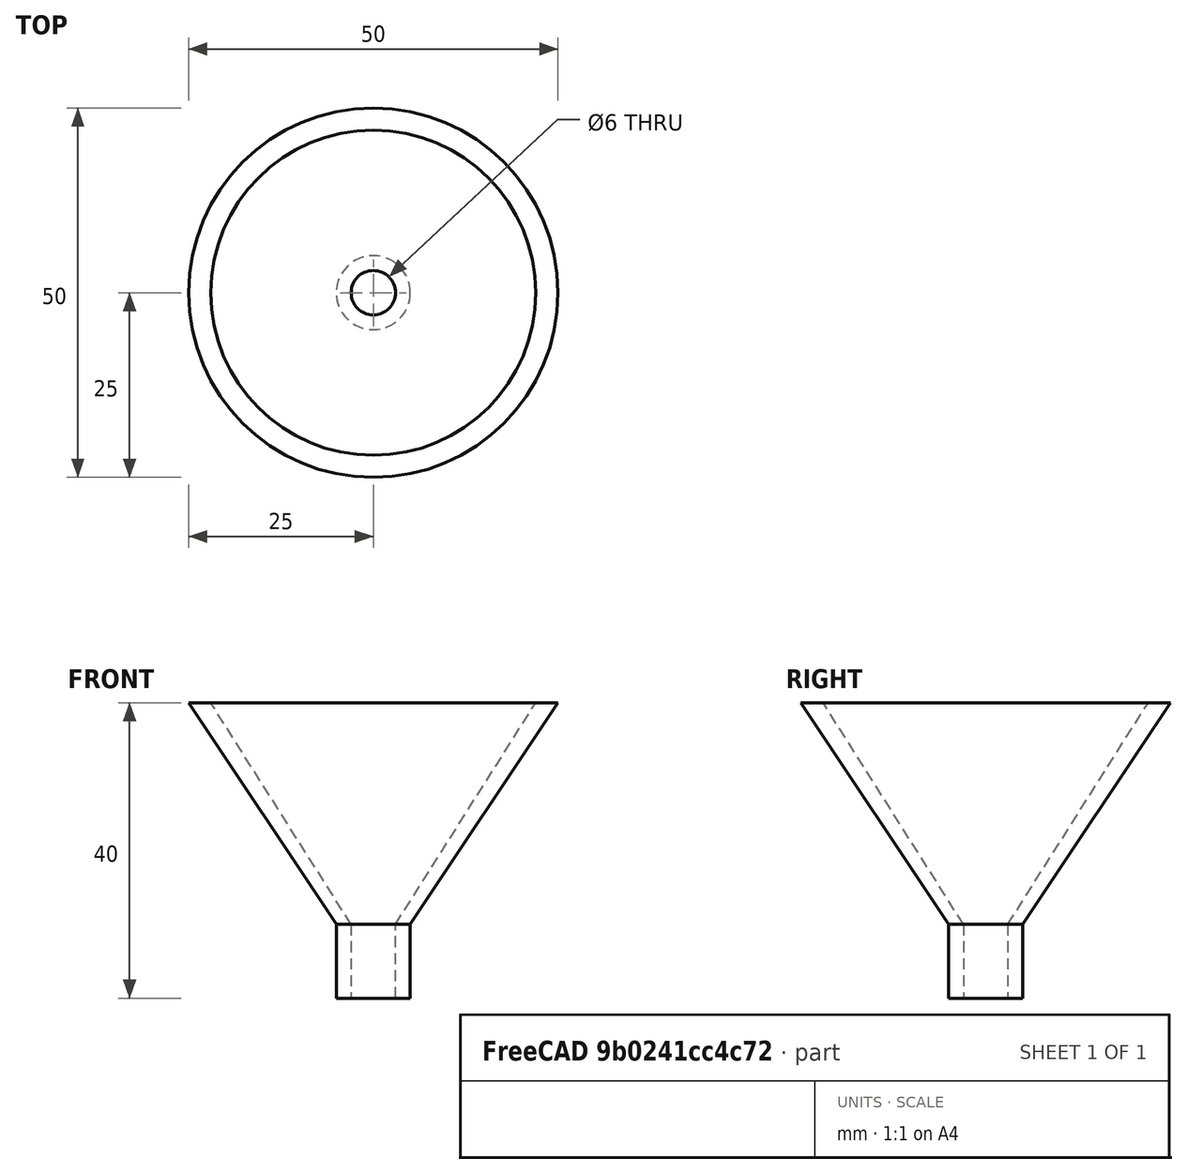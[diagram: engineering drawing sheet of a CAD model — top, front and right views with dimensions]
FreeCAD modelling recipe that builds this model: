
FCSTD DOCUMENT  (FreeCAD 0.20R29177 +426 (Git))
Label: Embudo
License: All rights reserved
LicenseURL: http://en.wikipedia.org/wiki/All_rights_reserved
objects: Part::Cone×2, Part::Cut×2, Part::Cylinder×2
note: 6 computed .brp shape members not serialized (recipe doc carries the construction recipe); baked Part::Feature solids carry a one-line shape summary decoded from their .brp

FEATURE [Part::Cone] Cone  label="Cono"
  Angle = 360
  AttacherType = Attacher::AttachEngine3D
  Height = 30
  Radius1 = 5
  Radius2 = 25
FEATURE [Part::Cone] Cone001  label="Cono001"
  Angle = 360
  AttacherType = Attacher::AttachEngine3D
  Height = 30
  Radius1 = 3
  Radius2 = 22
FEATURE [Part::Cut] Cut
  Base = -> Cone
  Refine = true
  Tool = -> Cone001
FEATURE [Part::Cylinder] Cylinder  label="Cilindro"
  Angle = 360
  AttacherType = Attacher::AttachEngine3D
  FirstAngle = 0
  Height = 10
  Placement = pos=(0,0,-10) rot=(0,0,1;0rad)
  Radius = 5
  SecondAngle = 0
FEATURE [Part::Cylinder] Cylinder001  label="Cilindro001"
  Angle = 360
  AttacherType = Attacher::AttachEngine3D
  FirstAngle = 0
  Height = 10
  Placement = pos=(0,0,-10) rot=(0,0,1;0rad)
  Radius = 3
  SecondAngle = 0
FEATURE [Part::Cut] Cut001
  Base = -> Cylinder
  Refine = true
  Tool = -> Cylinder001
